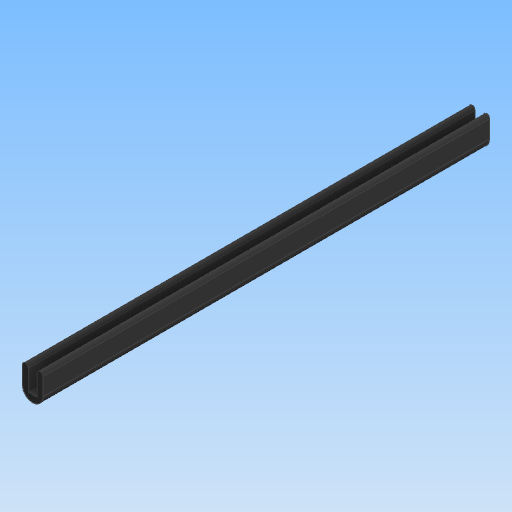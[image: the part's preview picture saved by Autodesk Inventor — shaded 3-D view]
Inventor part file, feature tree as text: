
AUTODESK INVENTOR PART (.ipt)
format: ipt  version: 2020 (Build 240168000, 168)  size: 103,936 bytes
history: native  units: mm
features: other x1, extrude x1
ambient origin geometry x8: Origin, YZ Plane, XZ Plane, XY Plane, X Axis, Y Axis, Z Axis, Center Point
bodies: Body1 (feature_tree)
feature tree (2):
  other  "實體1"
  extrude  "擠出1"  Depth=6.0mm
